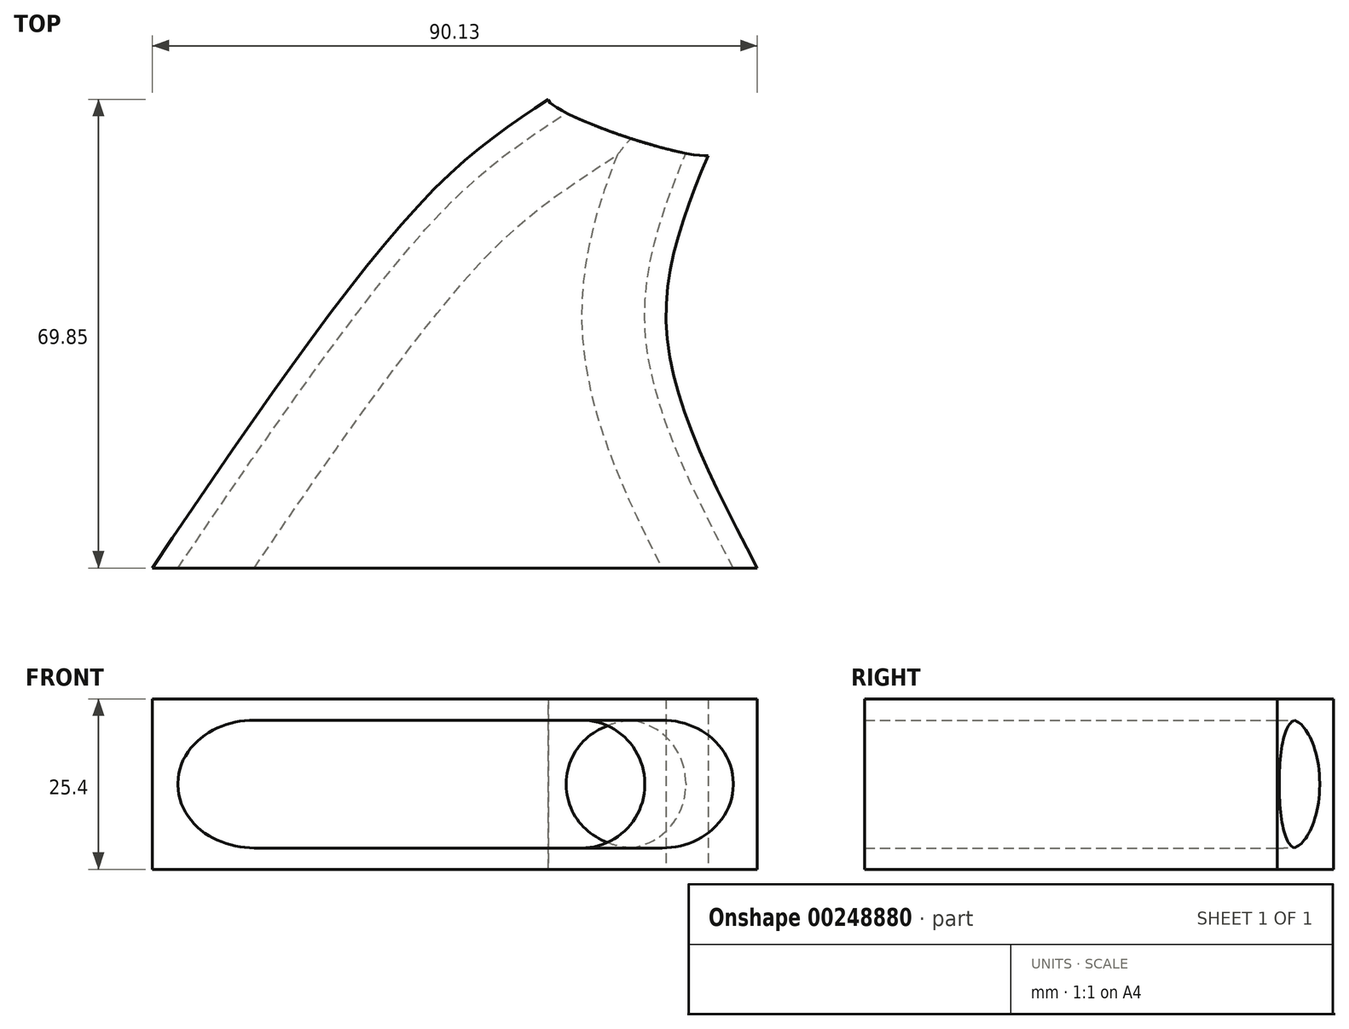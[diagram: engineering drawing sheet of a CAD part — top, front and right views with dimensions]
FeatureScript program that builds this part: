
annotation { "Feature Type Name" : "Feature", "Feature Type Description" : "" }
export const myFeature = defineFeature(function(context is Context, id is Id, definition is map)
    precondition{}
    {
        {
            var Q0;
            Q0=qCreatedBy(makeId("Top.planeOp"),FACE);
            var sketch = newSketch(context, id + "F0", { "sketchPlane" : qUnion([Q0])});
            skLineSegment(sketch, "E0", {"start": v(-41, -31.32) * mm, "end": v(49.12, -31.32) * mm});
            skFitSpline(sketch, "E1", {"points": [v(-41, -31.32) * mm, v(0, 24.1) * mm, v(18.03, 38.53) * mm], "startDerivative": vector(69.66, 102.75) * mm, "endDerivative": vector(46.33, 30.52) * mm});
            skFitSpline(sketch, "E2", {"points": [v(49.12, -31.32) * mm, v(35.6, 4.28) * mm, v(41.9, 30.42) * mm], "startDerivative": vector(-35.4, 67.76) * mm, "endDerivative": vector(22.65, 55.35) * mm});
            skEllipse(sketch, "E3", {"center": v(30.2, 34.47) * mm, "majorRadius": 12.83 * mm, "minorRadius": 1.67 * mm, "majorAxis": v(-0.95, 0.32)});
            skSolve(sketch);
        }
        {
            var Q0;
            {var subQ0=sQuery(id+"F0.wireOp",EDGE,"E0");Q0=makeQuery(id+"F0.imprint","IMPRINT",FACE,{"disambiguationData":[TD([[makeQuery(id+"F0.imprint","IMPRINT",EDGE,{"derivedFrom":subQ0}),1.0]])]});}
            extrude(context, id + "F1", {"entities" : qUnion([Q0]), "depth" : 25.4 * mm});
        }
        {
            var Q0;
            Q0=makeQuery(id+"F1.opExtrude","SWEPT_FACE",FACE,{"disambiguationData":[OSD([sQuery(id+"F0.wireOp",EDGE,"E0")])]});
            var Q1;
            Q1=makeQuery(id+"F1.opExtrude","SWEPT_FACE",FACE,{"disambiguationData":[OSD([sQuery(id+"F0.wireOp",EDGE,"E3")])]});
            var Q2;
            Q2=makeQuery(id+"F1.opExtrude","SWEPT_BODY",BODY,{"disambiguationData":[OSD([sQuery(id+"F0.wireOp",EDGE,"E0"),sQuery(id+"F0.wireOp",EDGE,"E1"),sQuery(id+"F0.wireOp",EDGE,"E2"),sQuery(id+"F0.wireOp",EDGE,"E3")])]});
            shell(context, id + "F2", {"entities" : qUnion([Q0, Q1]), "parts" : qUnion([Q2]), "thickness" : 3.17 * mm});
        }
        {
            var Q0;
            {var subQ0=sQuery(id+"F0.wireOp",EDGE,"E1");Q0=makeQuery(id+"F2.opShell","OFFSET_EDGE",EDGE,{"disambiguationData":[OSD([subQ0]),TDD([makeQuery(id+"F1.opExtrude","CAP_EDGE",EDGE,{"disambiguationData":[OSD([subQ0])],"isStart":true})])]});}
            var Q1;
            {var subQ0=sQuery(id+"F0.wireOp",EDGE,"E1");Q1=makeQuery(id+"F2.opShell","OFFSET_EDGE",EDGE,{"disambiguationData":[OSD([subQ0]),TDD([makeQuery(id+"F1.opExtrude","CAP_EDGE",EDGE,{"disambiguationData":[OSD([subQ0])],"isStart":false})])]});}
            var Q2;
            {var subQ0=sQuery(id+"F0.wireOp",EDGE,"E2");Q2=makeQuery(id+"F2.opShell","OFFSET_EDGE",EDGE,{"disambiguationData":[OSD([subQ0]),TDD([makeQuery(id+"F1.opExtrude","CAP_EDGE",EDGE,{"disambiguationData":[OSD([subQ0])],"isStart":true})])]});}
            var Q3;
            {var subQ0=sQuery(id+"F0.wireOp",EDGE,"E2");Q3=makeQuery(id+"F2.opShell","OFFSET_EDGE",EDGE,{"disambiguationData":[OSD([subQ0]),TDD([makeQuery(id+"F1.opExtrude","CAP_EDGE",EDGE,{"disambiguationData":[OSD([subQ0])],"isStart":false})])]});}
            fillet(context, id + "F3", {"entities" : qUnion([Q0, Q1, Q2, Q3]), "radius" : 9.4 * mm, "tangentPropagation" : true, "allowEdgeOverflow" : false});
        }
    });
